# Revit family: Lighting Fixture_Sylvania_Expospot 70 Fixed_Ceiling Recessed
name_source: partatom
category: Lighting Fixtures
revit_build: Autodesk Revit 2016 (Build: 20161004_0715(x64)
units: mm (PartAtom-declared; Revit-internal decimal feet)

## family parameters
Cut with Voids When Loaded = No
Host = Face
Light Source = Yes
OmniClass Number = 23.80.70.11.17
OmniClass Title = Specialized Lighting by Location or Use
Part Type = Normal
Room Calculation Point = No
Round Connector Dimension = Use Diameter
Shared = No

## types (11) — shared parameters
Apparent Load = 21 VA
Assembly Code = D5020200
Average Life = 50 000h
Body Material = Aluminum_Sylvania_Expospot_White
Color Filter = 16777215
Colour Variation Initial = 3SDCM
Control Gear Mounting = Remote
Control Gear Required = No
Control Gear Type = Electronic
Cooling Big Axis = 43 mm  [stored 0.141076 ft]
Cooling Material = Plastic_Sylvania_Expospot_Black
Cooling Small Axis = 32 mm  [stored 0.104987 ft]
Cutout Diameter = 100 mm  [stored 0.328084 ft]
Description = Specifically designed for Retail and Display applications. I.e. Supermarkets, Fashion Retail, Department stores. Build around a 70mm reflector and lens combination.
Diameter = 110 mm  [stored 0.360892 ft]
Dimmable = N
Dimming Lamp Color Temperature Shift = <None>
Drive Current = 500mA
Electrical Protection = Class II
Emit Shape Visible in Rendering = No
Emit from Circle Diameter = 86 mm  [stored 0.282152 ft]
Glow Wire Test = 850 °C
Height = 101 mm  [stored 0.331365 ft]
IK Rating = IK02
IP Rating = IP20
Inrush Current = 28 A
Inrush Duration = 139µs
LOR = 100%
Lamp = LED
Lamp Power Factor = 0.9
Manufacturer = Feilo Sylvania
Max. Luminaires per 10A B Breaker = 19
Max. Luminaires per 10A C Breaker = 31
Max. Luminaires per 13A B Breaker = 25
Max. Luminaires per 13A C Breaker = 41
Max. Luminaires per 16A B Breaker = 31
Max. Luminaires per 16A C Breaker = 51
Max. Luminaires per 20A B Breaker = 42
Max. Luminaires per 20A C Breaker = 70
Nominal Frequency = 50/60Hz
Photobiological Risk Group = RG1
Product Family = EXPOSPOT 70 FIXED
Product Page URL = http://www.sylvania-lighting.com
Radius = 55 mm  [stored 0.180446 ft]
Reflector Material = Aluminum_Sylvania_Expospot_Polished
Tilt Angle = -90°
Total Power Consumption = 21 W
URL = http://www.sylvania-lighting.com
Voltage = 240 V
Voltage Comments = 220-240V~
Weight = 1 kg
zero-valued in all types: Default Elevation

## per-type parameters (varying)
| type | Beam Angle | CRI | Diffuser Material | Photometric Web File | Product Code |
| EXPOSPOT 70 FIX 90 4K WB WHT | 52° | 90Ra | Acrylic_Sylvania_Expospot_4000K | 0060236.ies | 0060236 |
| EXPOSPOT 70 FIX 90 4K MB WHT | 42° | 90Ra | Acrylic_Sylvania_Expospot_4000K | 0060235.ies | 0060235 |
| EXPOSPOT 70 FIX 90 4K NB WHT | 24° | 90Ra | Acrylic_Sylvania_Expospot_4000K | 0060234.ies | 0060234 |
| EXPOSPOT 70 FIX 90 3K WB WHT | 53° | 90Ra | Acrylic_Sylvania_Expospot_3000K | 0060233.ies | 0060233 |
| EXPOSPOT 70 FIX 90 3K MB WHT | 42° | 90Ra | Acrylic_Sylvania_Expospot_3000K | 0060232.ies | 0060232 |
| EXPOSPOT 70 FIX 90 3K NB WHT | 25° | 90Ra | Acrylic_Sylvania_Expospot_3000K | 0060231.ies | 0060231 |
| EXPOSPOT 70 FIX 80 4K WB WHT | 54° | 80Ra | Acrylic_Sylvania_Expospot_4000K | 0060230.ies | 0060230 |
| EXPOSPOT 70 FIX 80 4K MB WHT | 42° | 80Ra | Acrylic_Sylvania_Expospot_4000K | 0060229.ies | 0060229 |
| EXPOSPOT 70 FIX 80 4K NB WHT | 25° | 80Ra | Acrylic_Sylvania_Expospot_4000K | 0060228.ies | 0060228 |
| EXPOSPOT 70 FIX 80 3K WB WHT | 54° | 80Ra | Acrylic_Sylvania_Expospot_3000K | 0060227.ies | 0060227 |
| EXPOSPOT 70 FIX 80 3K MB WHT | 43° | 80Ra | Acrylic_Sylvania_Expospot_3000K | 0060226.ies | 0060226 |

note: column(s) folded — value = type name in every type: Model

note: [stored X ft] marks values corroborated as IEEE doubles in the binary element streams (Revit-internal decimal feet)

## geometry (parser evidence)
native form markers: Sweep x2
no freeform markers — native parametric forms only
